# Revit family: SFHT Filter
name_source: partatom
category: Mechanical Equipment
units: mm (PartAtom-declared; Revit-internal decimal feet)

## family parameters
Always vertical = Yes
Classification = None
Cut with Voids When Loaded = No
OmniClass Number = 23.65.50.11
OmniClass Title = Water Treatment
Part Type = Normal
Room Calculation Point = No
Round Connector Dimension = Use Radius
Shared = No
Work Plane-Based = No

## types (6) — shared parameters
Assembly Code = D2090400
Black = Fluidra SFHT Base
Description = SFHT Commercial Horizontal Sand Filter
Flange = Fluidra SFHT Flange
Fluidra_Description = SFHT Commercial Horizontal Sand Filter
Fluidra_Manufacturer = Fluidra
Fluidra_Max_Filtration_Rate = 20 GPM/ft²
Fluidra_Max_Working_Pressure = 50.00 psi
Fluidra_Number_of_Flange_Bolts = 8
Glass = Fluidra SFHT Glass
Manufacturer = Fluidra
Tank = Fluidra Filter Body

## per-type parameters (varying)
- SFHT4272: A=41 13/16"; B=31 1/2"; Base=SFHT42 Base; C=95 5/16"; D=36 3/8"; Drain Cap1=24 5/16"; Drain Cap2=14 1/2"; E=38 1/4"; F=19 3/4"; Flange Adapter=Jandy_Flange_Adapter(6in) : Jandy_Flange_Adapter; Flange Connector=Flange(6in); Flange Gasket=Jandy_Flange_Gasket(6in); Flange Radius2=3 1/2"; Flange Ring=Jandy_Flange_Ring(6in) : Jandy_Flange_Ring; Flange Size=6"; Fluidra_Approximate_Operating_Weight=6714.00 lb; Fluidra_Filtration_Area=21.00 ft²; Fluidra_Freeboard=8 7/8"; Fluidra_Max_Flow_Rate=420 GPM; Fluidra_Min_Backwash_Flow_Rate=105 GPM; Fluidra_Sand_Required=2700.00 lb; Fluidra_Six_Hour_Capacity=151200.0 gal; Fluidra_Weight (empty)=729.00 lb; G=7 1/2"; H=32 1/2"; I=51"; Tank Radius=20 29/32"
- SFHT3461: A=34 1/2"; B=31 1/4"; Base=SFHT34 Base; C=71 1/2"; D=24"; Drain Cap1=28 5/16"; Drain Cap2=13"; E=23 1/2"; F=13 1/2"; Flange Adapter=Jandy_Flange_Adapter(4in); Flange Connector=Flange(4in); Flange Gasket=Jandy_Flange_Gasket(4in); Flange Radius2=2 1/2"; Flange Ring=Jandy_Flange_Ring(4in); Flange Size=4"; Fluidra_Approximate_Operating_Weight=3388.00 lb; Fluidra_Filtration_Area=13.50 ft²; Fluidra_Freeboard=7 3/8"; Fluidra_Max_Flow_Rate=270 GPM; Fluidra_Min_Backwash_Flow_Rate=68 GPM; Fluidra_Sand_Required=1400.00 lb; Fluidra_Six_Hour_Capacity=97200.0 gal; Fluidra_Weight (empty)=535.00 lb; G=9 7/8"; H=23 3/4"; I=42"; Tank Radius=17 1/4"
- SFHT4296: A=42 7/16"; B=31 1/2"; Base=SFHT42 Base; C=101 7/8"; D=49 7/8"; Drain Cap1=34 5/16"; Drain Cap2=14 1/2"; E=30 7/8"; F=21 1/4"; Flange Adapter=Jandy_Flange_Adapter(6in) : Jandy_Flange_Adapter; Flange Connector=Flange(6in); Flange Gasket=Jandy_Flange_Gasket(6in); Flange Radius2=3 1/2"; Flange Ring=Jandy_Flange_Ring(6in) : Jandy_Flange_Ring; Flange Size=6"; Fluidra_Approximate_Operating_Weight=8046.00 lb; Fluidra_Filtration_Area=26.00 ft²; Fluidra_Freeboard=8 7/8"; Fluidra_Max_Flow_Rate=520 GPM; Fluidra_Min_Backwash_Flow_Rate=130 GPM; Fluidra_Sand_Required=3200.00 lb; Fluidra_Six_Hour_Capacity=187200.0 gal; Fluidra_Weight (empty)=810.00 lb; G=7 1/2"; H=42 1/2"; I=51"; Tank Radius=21 7/32"
- SFHT3472: A=34 7/8"; B=31 1/4"; Base=SFHT34 Base; C=79 5/8"; D=20 7/8"; Drain Cap1=34 5/16"; Drain Cap2=13"; E=33 1/4"; F=16 1/8"; Flange Adapter=Jandy_Flange_Adapter(6in) : Jandy_Flange_Adapter; Flange Connector=Flange(6in); Flange Gasket=Jandy_Flange_Gasket(6in); Flange Radius2=3 1/2"; Flange Ring=Jandy_Flange_Ring(6in) : Jandy_Flange_Ring; Flange Size=6"; Fluidra_Approximate_Operating_Weight=3805.00 lb; Fluidra_Filtration_Area=15.30 ft²; Fluidra_Freeboard=7 3/8"; Fluidra_Max_Flow_Rate=306 GPM; Fluidra_Min_Backwash_Flow_Rate=77 GPM; Fluidra_Sand_Required=1600.00 lb; Fluidra_Six_Hour_Capacity=110160.0 gal; Fluidra_Weight (empty)=606.00 lb; G=9 7/8"; H=29 1/8"; I=41 7/8"; Tank Radius=17 7/16"
- SFHT3484: A=34 7/8"; B=31 1/4"; Base=SFHT34 Base; C=96 1/2"; D=47 1/2"; Drain Cap1=34 5/16"; Drain Cap2=13"; E=28 3/4"; F=20 1/2"; Flange Adapter=Jandy_Flange_Adapter(6in) : Jandy_Flange_Adapter; Flange Connector=Flange(6in); Flange Gasket=Jandy_Flange_Gasket(6in); Flange Radius2=3 1/2"; Flange Ring=Jandy_Flange_Ring(6in) : Jandy_Flange_Ring; Flange Size=6"; Fluidra_Approximate_Operating_Weight=4743.00 lb; Fluidra_Filtration_Area=19.30 ft²; Fluidra_Freeboard=7 3/8"; Fluidra_Max_Flow_Rate=386 GPM; Fluidra_Min_Backwash_Flow_Rate=97 GPM; Fluidra_Sand_Required=2000.00 lb; Fluidra_Six_Hour_Capacity=138960.0 gal; Fluidra_Weight (empty)=643.00 lb; G=9 7/8"; H=40 1/8"; I=41 7/8"; Tank Radius=17 7/16"
- SFHT4284: A=42 7/16"; B=31 1/2"; Base=SFHT42 Base; C=95 5/16"; D=36 3/8"; Drain Cap1=34 5/16"; Drain Cap2=14 1/2"; E=38 1/4"; F=20 1/4"; Flange Adapter=Jandy_Flange_Adapter(6in) : Jandy_Flange_Adapter; Flange Connector=Flange(6in); Flange Gasket=Jandy_Flange_Gasket(6in); Flange Radius2=3 1/2"; Flange Ring=Jandy_Flange_Ring(6in) : Jandy_Flange_Ring; Flange Size=6"; Fluidra_Approximate_Operating_Weight=7643.00 lb; Fluidra_Filtration_Area=23.00 ft²; Fluidra_Freeboard=8 7/8"; Fluidra_Max_Flow_Rate=460 GPM; Fluidra_Min_Backwash_Flow_Rate=115 GPM; Fluidra_Sand_Required=3100.00 lb; Fluidra_Six_Hour_Capacity=165600.0 gal; Fluidra_Weight (empty)=781.00 lb; G=7 1/2"; H=40"; I=51"; Tank Radius=21 7/32"

note: column(s) folded — value = type name in every type: Fluidra_Model, Model

## geometry (parser evidence)
native form markers: Sweep x43
no freeform markers — native parametric forms only
